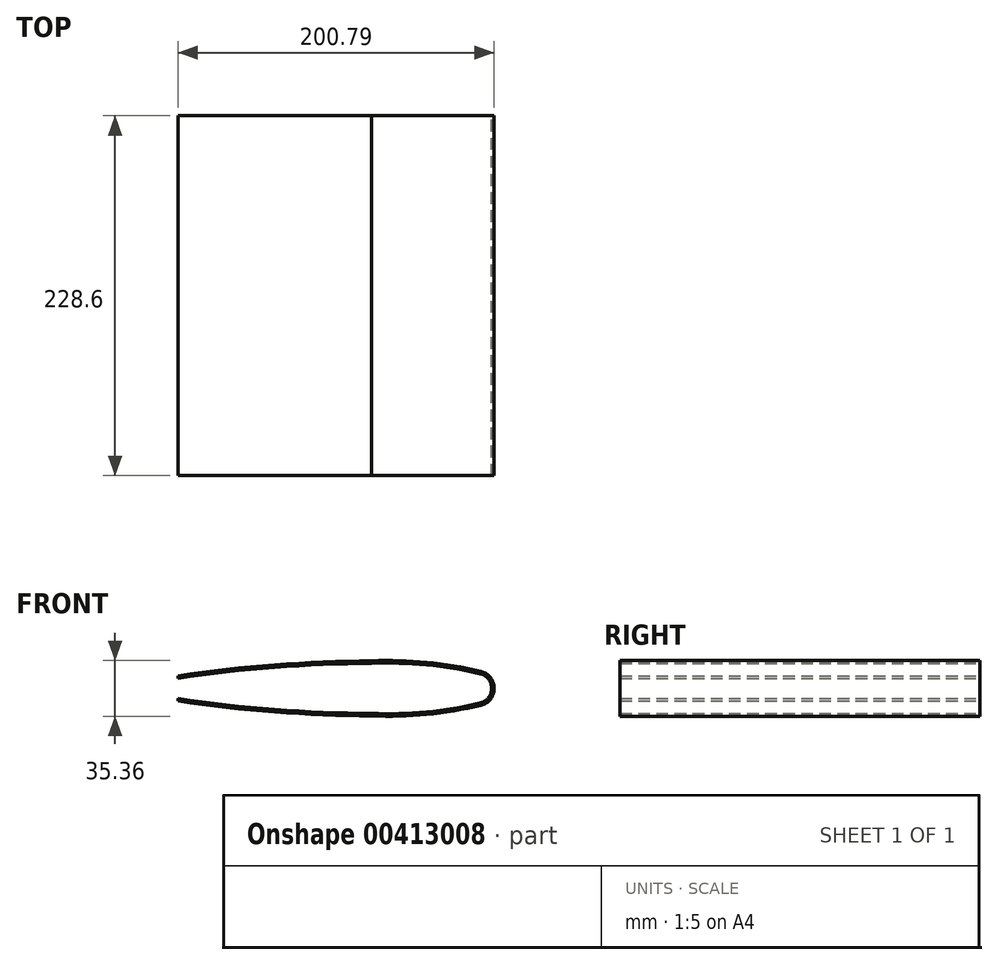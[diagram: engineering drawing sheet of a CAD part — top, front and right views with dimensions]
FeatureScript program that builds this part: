
annotation { "Feature Type Name" : "Feature", "Feature Type Description" : "" }
export const myFeature = defineFeature(function(context is Context, id is Id, definition is map)
    precondition{}
    {
        {
            var Q0;
            Q0=qCreatedBy(makeId("Front.planeOp"),FACE);
            var sketch = newSketch(context, id + "F0", { "sketchPlane" : qUnion([Q0])});
            skLineSegment(sketch, "E0", {"start": v(-107.84, 6.5) * mm, "end": v(-107.84, 8.08) * mm});
            skLineSegment(sketch, "E1", {"start": v(15.17, 15.88) * mm, "end": v(15.17, 17.46) * mm});
            skArc(sketch, "E2", {"start": v(15.17, 17.46) * mm, "mid": v(-46.5, 14.97) * mm, "end": v(-107.84, 8.08) * mm});
            skArc(sketch, "E3", {"start": v(84.4, -10.81) * mm, "mid": v(92.95, 0) * mm, "end": v(84.4, 10.81) * mm});
            skLineSegment(sketch, "E4", {"start": v(-107.84, -6.5) * mm, "end": v(-107.84, -8.08) * mm});
            skLineSegment(sketch, "E5", {"start": v(15.17, -15.87) * mm, "end": v(15.17, -17.46) * mm});
            skArc(sketch, "E6", {"start": v(-107.84, -8.08) * mm, "mid": v(-46.5, -14.97) * mm, "end": v(15.17, -17.46) * mm});
            skArc(sketch, "E7", {"start": v(15.17, -17.46) * mm, "mid": v(50.02, -16.52) * mm, "end": v(84.4, -10.81) * mm});
            skArc(sketch, "E8.trimOffspring", {"start": v(84.4, 10.81) * mm, "mid": v(50.02, 16.52) * mm, "end": v(15.17, 17.46) * mm});
            skArc(sketch, "E9", {"start": v(15.17, 15.87) * mm, "mid": v(-46.5, 13.38) * mm, "end": v(-107.84, 6.5) * mm});
            skArc(sketch, "E10", {"start": v(-107.84, -6.5) * mm, "mid": v(-46.5, -13.38) * mm, "end": v(15.17, -15.87) * mm});
            skArc(sketch, "E11", {"start": v(15.17, -15.88) * mm, "mid": v(49.83, -14.93) * mm, "end": v(84.03, -9.27) * mm});
            skArc(sketch, "E12", {"start": v(84.03, 9.27) * mm, "mid": v(49.83, 14.93) * mm, "end": v(15.17, 15.88) * mm});
            skArc(sketch, "E13", {"start": v(84.03, -9.27) * mm, "mid": v(91.37, 0) * mm, "end": v(84.03, 9.27) * mm});
            skSolve(sketch);
        }
        {
            var Q0;
            Q0 = qSketchRegion(id + "F0", true);
            extrude(context, id + "F1", {"entities" : qUnion([Q0]), "depth" : 228.6 * mm});
        }
    });
